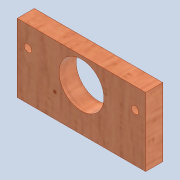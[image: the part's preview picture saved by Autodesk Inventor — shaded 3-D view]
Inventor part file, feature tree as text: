
AUTODESK INVENTOR PART (.ipt)
format: ipt  version: 2020 (Build 240168000, 168)  size: 140,288 bytes
history: native  units: mm
features: extrude x3, sketch x3, direct_edit x1, move_body x1
ambient origin geometry x8: Origin, YZ Plane, XZ Plane, XY Plane, X Axis, Y Axis, Z Axis, Center Point
bodies: Solid1 (feature_tree)
feature tree (8):
  extrude  "Extrusion1"  Depth=60.0mm
  extrude  "Extrusion2"  Depth=8.0mm
  extrude  "Extrusion3"  TaperAngle=0.0deg  [1 undecoded]
  direct_edit  "Direct Edit1"
  sketch  "Sketch1"  dims[d0=60.0mm d1=35.0mm]
  sketch  "Sketch2"  dims[d2=8.0mm d3=0.0mm d4=5.0mm]
  sketch  "Sketch3"  dims[d5=21.0mm d6=0.0mm d7=0.0mm d9=3.5mm d10=3.5mm d11=10.0mm d12=2.5mm d13=5.0mm d14=5.0mm d15=0.0mm d16=0.0mm d17=21.0mm d18=15.0mm d19=0.0mm d20=0.0mm d21=-3.0mm]
  move_body  "Move1"
note: 1 required parameter value undecoded (feature->parameter linkage not recoverable at this tier; creation-order binding heuristic only, values carry confidence <= 0.55)
